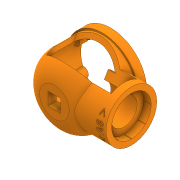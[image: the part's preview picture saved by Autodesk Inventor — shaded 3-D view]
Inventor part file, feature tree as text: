
AUTODESK INVENTOR PART (.ipt)
format: ipt  version: 2020 (Build 240168000, 168)  size: 911,872 bytes
history: native  units: in
note: dims shown in document units (in); Inventor stores cm internally (conversion verified against a paired STEP export)
features: sketch x27, extrude x24, plane x8, projected_geometry x6, chamfer x5, revolve x1, fillet x1, emboss x1
ambient origin geometry x8: Origin, YZ Plane, XZ Plane, XY Plane, X Axis, Y Axis, Z Axis, Center Point
bodies: Solid1 (feature_tree)
feature tree (73):
  extrude  "Extrusion1"  Depth=0.315in TaperAngle=0.0deg
  chamfer  "Chamfer1"  Distance=0.315in
  extrude  "Extrusion2"  Depth=2.3622in TaperAngle=360.0deg
  extrude  "Extrusion3"  Depth=0.315in TaperAngle=0.0deg
  extrude  "Extrusion4"  Depth=0.1575in TaperAngle=0.0deg
  extrude  "Extrusion5"  Depth=1.2598in TaperAngle=0.0deg
  revolve  "Revolution1"  [1 undecoded]
  plane  "Work Plane1"
  extrude  "Extrusion6"  Depth=0.1575in
  plane  "Work Plane2"
  plane  "Work Plane3"
  extrude  "Extrusion8"  [1 undecoded]
  extrude  "Extrusion9"  Depth=0.1575in TaperAngle=0.0deg
  chamfer  "Chamfer3"  Distance=1.8898in
  extrude  "Extrusion10"  Depth=1.8898in
  plane  "Work Plane4"
  extrude  "Extrusion11"  Depth=0.315in TaperAngle=0.0deg
  extrude  "Extrusion12"  Depth=0.2756in
  extrude  "Extrusion13"  Depth=3.1496in TaperAngle=360.0deg
  plane  "Work Plane5"
  extrude  "Extrusion15"  [1 undecoded]
  extrude  "Extrusion16"  Depth=0.4764in
  plane  "Work Plane6"
  extrude  "Extrusion18"  Depth=0.315in
  extrude  "Extrusion20"  Depth=0.315in
  extrude  "Extrusion21"  TaperAngle=60.0deg  [1 undecoded]
  extrude  "Extrusion22"  TaperAngle=0.0deg  [1 undecoded]
  chamfer  "Chamfer34"  Distance=2.3622in
  chamfer  "Chamfer35"  Distance=0.1969in
  fillet  "Fillet1"  [1 undecoded]
  plane  "Work Plane7"
  emboss  "Emboss1"
  chamfer  "Chamfer36"  Distance=0.1969in
  sketch  "Sketch25"  dims[d178=0.315in]
  plane  "Work Plane8"
  extrude  "Extrusion23"  Depth=0.0984in TaperAngle=0.0deg
  extrude  "Extrusion24"  Depth=0.0984in TaperAngle=0.0deg
  extrude  "Extrusion25"  Depth=0.315in
  extrude  "Extrusion26"  Depth=0.315in
  extrude  "Extrusion27"  Depth=0.315in
  extrude  "Extrusion28"  Depth=0.0394in TaperAngle=0.0deg
  sketch  "Sketch1"  dims[d0=0.4724in d1=0.315in d2=0.0in d3=0.315in d4=0.125in d5=0.0137in]
  sketch  "Sketch2"  dims[d6=0.0157in d7=2.3622in d9=360.0deg]
  sketch  "Sketch3"  dims[d11=0.315in d12=0.0in d13=0.0197in d14=0.0in]
  projected_geometry  "Projected Loop1"
  sketch  "Sketch4"  dims[d15=2.5591in d16=0.1575in d17=0.0in]
  sketch  "Sketch5"  dims[d18=0.1575in d19=1.2598in d20=0.0in]
  sketch  "Sketch6"  dims[d21=1.1024in d22=0.5512in]
  sketch  "Sketch7"  dims[d23=0.8465in d24=0.1575in]
  sketch  "Sketch9"  dims[d25=90.0deg d26=-2.1063in]
  sketch  "Sketch10"  dims[d27=0.1575in d28=0.1575in d29=0.0in d33=-0.1575in d41=1.8898in]
  sketch  "Sketch11"  dims[d42=1.2795in d43=1.8898in]
  sketch  "Sketch12"  dims[d44=0.2165in d45=0.315in d46=0.0in]
  sketch  "Sketch13"  dims[d47=1.1811in d48=0.0in d49=0.2756in d50=0.125in d51=0.0137in]
  sketch  "Sketch14"  dims[d52=0.0157in d53=3.1496in d55=360.0deg]
  sketch  "Sketch16"  dims[d57=0.2756in d58=0.0in d59=-0.2756in]
  sketch  "Sketch17"  dims[d61=0.9843in d62=0.0in d63=0.4764in]
  sketch  "Sketch19"  dims[d64=0.315in d65=0.0in d66=0.0787in]
  projected_geometry  "Projected Loop2"
  projected_geometry  "Projected Loop3"
  sketch  "Sketch21"  dims[d73=0.315in d74=0.0in d166=0.9843in]
  sketch  "Sketch22"  dims[d171=-0.2756in d172=60.0deg]
  sketch  "Sketch23"  dims[d173=60.0deg d174=0.0in]
  projected_geometry  "Projected Loop4"
  sketch  "Sketch24"  dims[d175=0.0in d176=2.3622in d177=0.0in]
  sketch  "Sketch28"  dims[d179=0.2067in]
  sketch  "Sketch29"  dims[d180=0.0787in]
  sketch  "Sketch30"  dims[d181=45.0deg d182=0.1969in d183=0.0in d187=-0.4921in d188=0.1969in d189=0.0in]
  projected_geometry  "Projected Loop5"
  sketch  "Sketch31"  dims[d193=0.315in d194=0.0984in d195=0.0in]
  sketch  "Sketch32"  dims[d196=0.2362in d197=0.0984in d198=0.0in]
  sketch  "Sketch33"  dims[d199=0.0984in d200=0.0in d201=0.0591in d202=0.125in d203=0.0137in d204=0.0591in d205=0.125in d206=0.0137in d207=0.0197in d209=0.0394in d210=0.0in d211=0.0787in d212=0.125in d213=0.0137in d214=2.126in d215=-0.1575in d217=0.4921in d218=0.0in d220=4.7244in d221=0.1083in d222=0.1575in d223=360.0deg d224=0.1969in d225=0.1969in d226=0.1969in d227=0.1969in d228=0.1969in d229=0.1969in d230=0.1969in d231=0.1969in d232=0.1969in d233=0.1969in d234=0.0787in d235=0.0787in d236=0.0787in d237=0.0787in d238=0.0787in d239=0.0787in d240=0.0787in d241=0.0787in d242=0.0787in d243=0.0787in d244=0.315in d245=0.0in d246=0.315in d247=0.0in d248=0.0591in d249=0.315in d250=0.0in d251=0.0394in d252=0.0in d253=0.4724in d254=0.4724in d255=0.315in d256=0.0in]
  projected_geometry  "Projected Loop6"
note: 6 required parameter values undecoded (feature->parameter linkage not recoverable at this tier; creation-order binding heuristic only, values carry confidence <= 0.55)